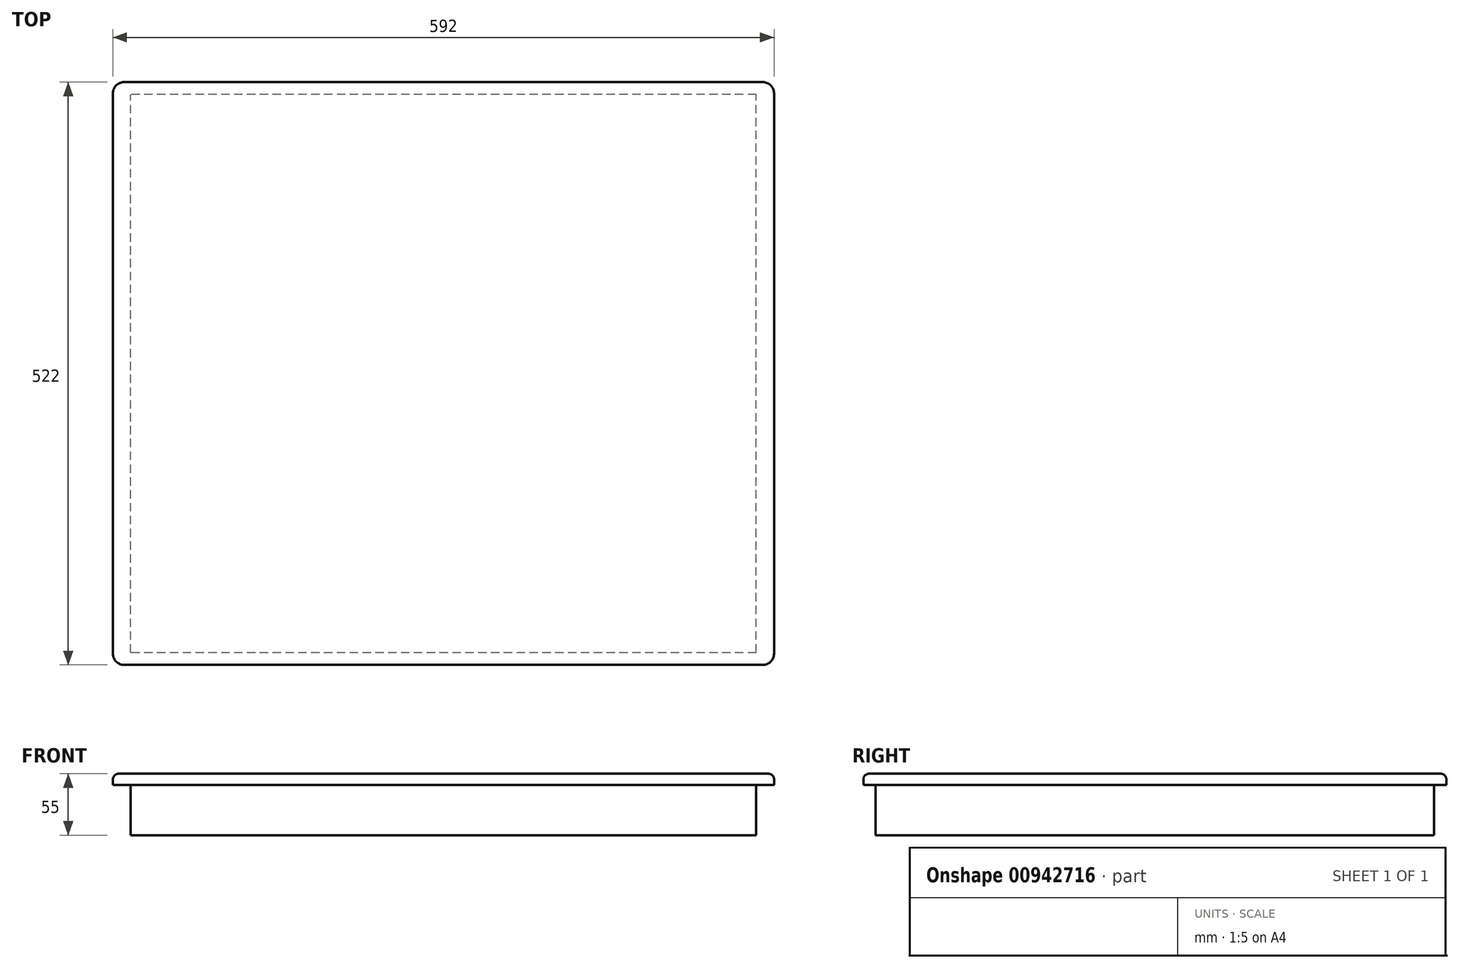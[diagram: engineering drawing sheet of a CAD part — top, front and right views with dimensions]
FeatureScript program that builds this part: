
annotation { "Feature Type Name" : "Feature", "Feature Type Description" : "" }
export const myFeature = defineFeature(function(context is Context, id is Id, definition is map)
    precondition{}
    {
        {
            var Q0;
            Q0=qCreatedBy(makeId("Top.planeOp"),FACE);
            var sketch = newSketch(context, id + "F0", { "sketchPlane" : qUnion([Q0])});
            skLineSegment(sketch, "E0.bottom", {"start": v(-286, 261) * mm, "end": v(286, 261) * mm});
            skLineSegment(sketch, "E0.top", {"start": v(-286, -261) * mm, "end": v(286, -261) * mm});
            skLineSegment(sketch, "E0.left", {"start": v(-296, 251) * mm, "end": v(-296, -251) * mm});
            skLineSegment(sketch, "E0.right", {"start": v(296, 251) * mm, "end": v(296, -251) * mm});
            skLineSegment(sketch, "E1", {"start": v(-296, 0) * mm, "end": v(0, 0) * mm, "construction": true});
            skLineSegment(sketch, "E2", {"start": v(0, 0) * mm, "end": v(296, 0) * mm, "construction": true});
            skLineSegment(sketch, "E3", {"start": v(0, -261) * mm, "end": v(0, 0) * mm, "construction": true});
            skLineSegment(sketch, "E4", {"start": v(0, 0) * mm, "end": v(0, 261) * mm, "construction": true});
            skPoint(sketch, "E5.visualSharp", {"position": v(296, 261) * mm});
            skArc(sketch, "E5.filletArc", {"start": v(296, 251) * mm, "mid": v(293.07, 258.07) * mm, "end": v(286, 261) * mm});
            skPoint(sketch, "E6.visualSharp", {"position": v(296, -261) * mm});
            skArc(sketch, "E6.filletArc", {"start": v(286, -261) * mm, "mid": v(293.07, -258.07) * mm, "end": v(296, -251) * mm});
            skPoint(sketch, "E7.visualSharp", {"position": v(-296, -261) * mm});
            skArc(sketch, "E7.filletArc", {"start": v(-296, -251) * mm, "mid": v(-293.07, -258.07) * mm, "end": v(-286, -261) * mm});
            skPoint(sketch, "E8.visualSharp", {"position": v(-296, 261) * mm});
            skArc(sketch, "E8.filletArc", {"start": v(-286, 261) * mm, "mid": v(-293.07, 258.07) * mm, "end": v(-296, 251) * mm});
            skLineSegment(sketch, "E9.bottom", {"start": v(-280, 250) * mm, "end": v(280, 250) * mm});
            skLineSegment(sketch, "E9.top", {"start": v(-280, -250) * mm, "end": v(280, -250) * mm});
            skLineSegment(sketch, "E9.left", {"start": v(-280, 250) * mm, "end": v(-280, -250) * mm});
            skLineSegment(sketch, "E9.right", {"start": v(280, 250) * mm, "end": v(280, -250) * mm});
            skLineSegment(sketch, "E10", {"start": v(280, 135.74) * mm, "end": v(296, 135.74) * mm, "construction": true});
            skLineSegment(sketch, "E11", {"start": v(142.53, 250) * mm, "end": v(142.53, 261) * mm, "construction": true});
            skLineSegment(sketch, "E12", {"start": v(113.9, -250) * mm, "end": v(113.9, -261) * mm, "construction": true});
            skLineSegment(sketch, "E13", {"start": v(-280, -132.52) * mm, "end": v(-296, -132.52) * mm, "construction": true});
            skSolve(sketch);
        }
        {
            var Q0;
            Q0=makeQuery(id+"F0.imprint","IMPRINT",FACE,{"disambiguationData":[TD([[makeQuery(id+"F0.imprint","IMPRINT",EDGE,{"derivedFrom":sQuery(id+"F0.wireOp",EDGE,"E9.bottom")}),-1.0]])]});
            extrude(context, id + "F1", {"entities" : qUnion([Q0]), "oppositeDirection" : true, "depth" : 55 * mm, "offsetDistance" : 25 * mm});
        }
        {
            var Q0;
            Q0=makeQuery(id+"F0.imprint","IMPRINT",FACE,{"disambiguationData":[TD([[makeQuery(id+"F0.imprint","IMPRINT",EDGE,{"derivedFrom":sQuery(id+"F0.wireOp",EDGE,"E0.bottom")}),-1.0]])]});
            var Q1;
            Q1=makeQuery(id+"F0.imprint","IMPRINT",FACE,{"disambiguationData":[TD([[makeQuery(id+"F0.imprint","IMPRINT",EDGE,{"derivedFrom":sQuery(id+"F0.wireOp",EDGE,"E9.bottom")}),-1.0]])]});
            extrude(context, id + "F2", {"entities" : qUnion([Q0, Q1]), "operationType" : NewBodyOperationType.ADD, "oppositeDirection" : true, "depth" : 10 * mm, "offsetDistance" : 25 * mm});
        }
        {
            var Q0;
            Q0=makeQuery(id+"F2.boolean.opBoolean","MERGE",FACE,{"derivedFrom":[makeQuery(id+"F1.opExtrude","CAP_FACE",FACE,{"disambiguationData":[OSD([sQuery(id+"F0.wireOp",EDGE,"E9.bottom"),sQuery(id+"F0.wireOp",EDGE,"E9.top"),sQuery(id+"F0.wireOp",EDGE,"E9.left"),sQuery(id+"F0.wireOp",EDGE,"E9.right")])],"isStart":true}),makeQuery(id+"F2.opExtrude","CAP_FACE",FACE,{"disambiguationData":[OSD([sQuery(id+"F0.wireOp",EDGE,"E0.bottom"),sQuery(id+"F0.wireOp",EDGE,"E0.top"),sQuery(id+"F0.wireOp",EDGE,"E0.left"),sQuery(id+"F0.wireOp",EDGE,"E0.right"),sQuery(id+"F0.wireOp",EDGE,"E5.filletArc"),sQuery(id+"F0.wireOp",EDGE,"E6.filletArc"),sQuery(id+"F0.wireOp",EDGE,"E7.filletArc"),sQuery(id+"F0.wireOp",EDGE,"E8.filletArc")])],"isStart":true})]});
            fillet(context, id + "F3", {"entities" : qUnion([Q0]), "radius" : 5 * mm, "tangentPropagation" : true, "allowEdgeOverflow" : false});
        }
    });
